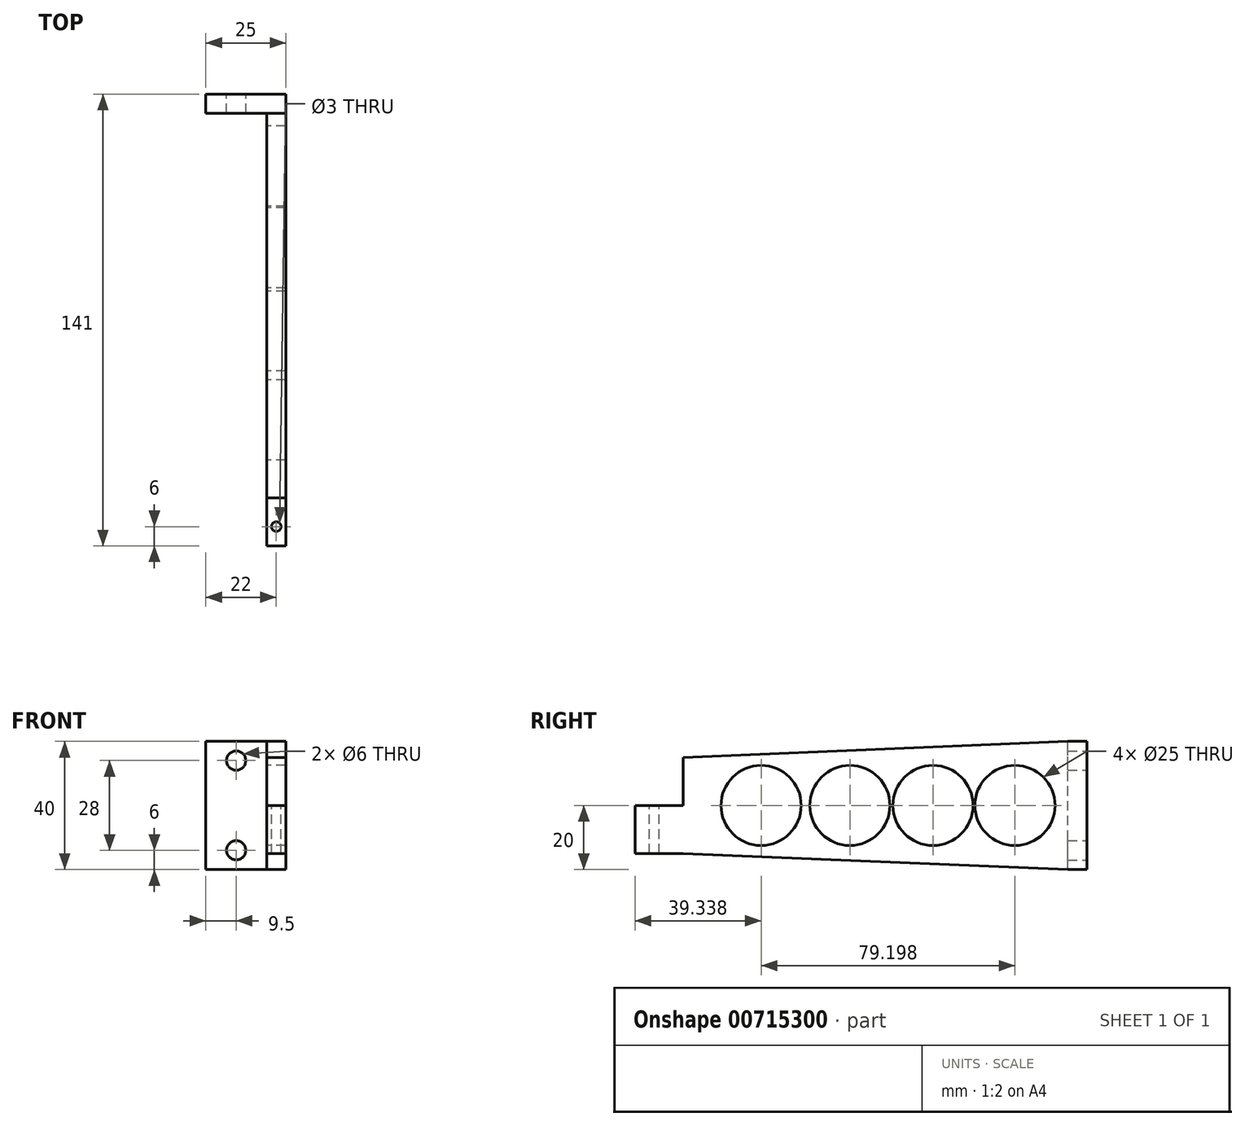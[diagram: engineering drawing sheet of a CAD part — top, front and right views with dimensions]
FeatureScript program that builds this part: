
annotation { "Feature Type Name" : "Feature", "Feature Type Description" : "" }
export const myFeature = defineFeature(function(context is Context, id is Id, definition is map)
    precondition{}
    {
        {
            var Q0;
            Q0=qCreatedBy(makeId("Front.planeOp"),FACE);
            var sketch = newSketch(context, id + "F0", { "sketchPlane" : qUnion([Q0])});
            skLineSegment(sketch, "E0.bottom", {"start": v(12.5, 20) * mm, "end": v(-12.5, 20) * mm});
            skLineSegment(sketch, "E0.top", {"start": v(12.5, -20) * mm, "end": v(-12.5, -20) * mm});
            skLineSegment(sketch, "E0.left", {"start": v(12.5, 20) * mm, "end": v(12.5, -20) * mm});
            skLineSegment(sketch, "E0.right", {"start": v(-12.5, 20) * mm, "end": v(-12.5, -20) * mm});
            skPoint(sketch, "E0.middle", {"position": v(0, 0) * mm});
            skLineSegment(sketch, "E1", {"start": v(6.5, 20) * mm, "end": v(6.5, -20) * mm, "construction": true});
            skLineSegment(sketch, "E2", {"start": v(6.5, 20) * mm, "end": v(-12.5, 20) * mm, "construction": true});
            skLineSegment(sketch, "E3", {"start": v(-3, -20) * mm, "end": v(-3, 20) * mm, "construction": true});
            skPoint(sketch, "E3.startSnap0", {"position": v(-3, 20) * mm});
            skLineSegment(sketch, "E4", {"start": v(-12.5, 14) * mm, "end": v(6.5, 14) * mm, "construction": true});
            skLineSegment(sketch, "E5", {"start": v(-12.5, -14) * mm, "end": v(6.5, -14) * mm, "construction": true});
            skCircle(sketch, "E6", {"center": v(-3, 14) * mm, "radius": 3 * mm});
            skCircle(sketch, "E7", {"center": v(-3, -14) * mm, "radius": 3 * mm});
            skSolve(sketch);
        }
        {
            var Q0;
            Q0=makeQuery(id+"F0.imprint","IMPRINT",FACE,{"disambiguationData":[TD([[makeQuery(id+"F0.imprint","IMPRINT",EDGE,{"derivedFrom":sQuery(id+"F0.wireOp",EDGE,"E0.bottom")}),1.0]])]});
            extrude(context, id + "F1", {"entities" : qUnion([Q0]), "depth" : 6 * mm, "offsetDistance" : 25.4 * mm});
        }
        {
            var Q0;
            Q0=makeQuery(id+"F1.opExtrude","CAP_FACE",FACE,{"disambiguationData":[OSD([sQuery(id+"F0.wireOp",EDGE,"E0.bottom"),sQuery(id+"F0.wireOp",EDGE,"E0.top"),sQuery(id+"F0.wireOp",EDGE,"E0.left"),sQuery(id+"F0.wireOp",EDGE,"E0.right")])],"isStart":false});
            var sketch = newSketch(context, id + "F2", { "sketchPlane" : qUnion([Q0])});
            skLineSegment(sketch, "E8", {"start": v(12.5, 20) * mm, "end": v(12.5, -20) * mm});
            skLineSegment(sketch, "E9", {"start": v(12.5, -20) * mm, "end": v(6.5, -20) * mm});
            skLineSegment(sketch, "E10", {"start": v(6.5, -20) * mm, "end": v(6.5, 20) * mm});
            skLineSegment(sketch, "E11", {"start": v(6.5, 20) * mm, "end": v(12.5, 20) * mm});
            skSolve(sketch);
        }
        {
            var Q0;
            Q0=makeQuery(id+"F2.imprint","IMPRINT",FACE,{"disambiguationData":[TD([[makeQuery(id+"F2.imprint","IMPRINT",EDGE,{"derivedFrom":sQuery(id+"F2.wireOp",EDGE,"E8")}),-1.0]])]});
            extrude(context, id + "F3", {"entities" : qUnion([Q0]), "operationType" : NewBodyOperationType.ADD, "depth" : 120 * mm, "offsetDistance" : 25.4 * mm});
        }
        {
            var Q0;
            Q0=makeQuery(id+"F3.opExtrude","SWEPT_FACE",FACE,{"disambiguationData":[OSD([sQuery(id+"F2.wireOp",EDGE,"E10")])]});
            var sketch = newSketch(context, id + "F4", { "sketchPlane" : qUnion([Q0])});
            skLineSegment(sketch, "E12", {"start": v(6, -20) * mm, "end": v(126, -15) * mm});
            skLineSegment(sketch, "E13", {"start": v(6, 20) * mm, "end": v(126, 15) * mm});
            skCircle(sketch, "E14", {"center": v(22.46, 0) * mm, "radius": 12.5 * mm});
            skCircle(sketch, "E15", {"center": v(48.04, 0) * mm, "radius": 12.5 * mm});
            skCircle(sketch, "E16", {"center": v(73.97, 0) * mm, "radius": 12.5 * mm});
            skCircle(sketch, "E17", {"center": v(101.66, 0) * mm, "radius": 12.5 * mm});
            skSolve(sketch);
        }
        {
            var Q0;
            {var subQ0=sQuery(id+"F4.wireOp",EDGE,"E13");Q0=makeQuery(id+"F4.imprint","IMPRINT",FACE,{"disambiguationData":[TD([[makeQuery(id+"F4.imprint","IMPRINT",EDGE,{"derivedFrom":subQ0}),1.0]])]});}
            var Q1;
            {var subQ0=sQuery(id+"F4.wireOp",EDGE,"E12");Q1=makeQuery(id+"F4.imprint","IMPRINT",FACE,{"disambiguationData":[TD([[makeQuery(id+"F4.imprint","IMPRINT",EDGE,{"derivedFrom":subQ0}),-1.0]])]});}
            var Q2;
            Q2=makeQuery(id+"F4.imprint","IMPRINT",FACE,{"disambiguationData":[TD([[makeQuery(id+"F4.imprint","IMPRINT",EDGE,{"derivedFrom":sQuery(id+"F4.wireOp",EDGE,"E17")}),1.0]])]});
            var Q3;
            Q3=makeQuery(id+"F4.imprint","IMPRINT",FACE,{"disambiguationData":[TD([[makeQuery(id+"F4.imprint","IMPRINT",EDGE,{"derivedFrom":sQuery(id+"F4.wireOp",EDGE,"E16")}),1.0]])]});
            var Q4;
            Q4=makeQuery(id+"F4.imprint","IMPRINT",FACE,{"disambiguationData":[TD([[makeQuery(id+"F4.imprint","IMPRINT",EDGE,{"derivedFrom":sQuery(id+"F4.wireOp",EDGE,"E15")}),1.0]])]});
            var Q5;
            Q5=makeQuery(id+"F4.imprint","IMPRINT",FACE,{"disambiguationData":[TD([[makeQuery(id+"F4.imprint","IMPRINT",EDGE,{"derivedFrom":sQuery(id+"F4.wireOp",EDGE,"E14")}),1.0]])]});
            extrude(context, id + "F5", {"entities" : qUnion([Q0, Q1, Q2, Q3, Q4, Q5]), "operationType" : NewBodyOperationType.REMOVE, "oppositeDirection" : true, "depth" : 25.4 * mm, "offsetDistance" : 25.4 * mm});
        }
        {
            var Q0;
            Q0=makeQuery(id+"F3.opExtrude","CAP_FACE",FACE,{"disambiguationData":[OSD([sQuery(id+"F2.wireOp",EDGE,"E8"),sQuery(id+"F2.wireOp",EDGE,"E9"),sQuery(id+"F2.wireOp",EDGE,"E10"),sQuery(id+"F2.wireOp",EDGE,"E11")])],"isStart":false});
            var sketch = newSketch(context, id + "F6", { "sketchPlane" : qUnion([Q0])});
            skLineSegment(sketch, "E18.bottom", {"start": v(12.5, 15) * mm, "end": v(6.5, 15) * mm});
            skLineSegment(sketch, "E18.top", {"start": v(12.5, 0) * mm, "end": v(6.5, 0) * mm});
            skLineSegment(sketch, "E18.left", {"start": v(12.5, 15) * mm, "end": v(12.5, 0) * mm});
            skLineSegment(sketch, "E18.right", {"start": v(6.5, 15) * mm, "end": v(6.5, 0) * mm});
            skSolve(sketch);
        }
        {
            var Q0;
            {var subQ0=sQuery(id+"F6.wireOp",EDGE,"E18.top");Q0=makeQuery(id+"F6.imprint","IMPRINT",FACE,{"disambiguationData":[TD([[makeQuery(id+"F6.imprint","IMPRINT",EDGE,{"derivedFrom":subQ0}),1.0]])]});}
            extrude(context, id + "F7", {"entities" : qUnion([Q0]), "operationType" : NewBodyOperationType.ADD, "depth" : 15 * mm, "offsetDistance" : 25.4 * mm});
        }
        {
            var Q0;
            Q0=makeQuery(id+"F7.opExtrude","SWEPT_FACE",FACE,{"disambiguationData":[OSD([sQuery(id+"F6.wireOp",EDGE,"E18.top")])]});
            var sketch = newSketch(context, id + "F8", { "sketchPlane" : qUnion([Q0])});
            skCircle(sketch, "E19", {"center": v(9.5, -135) * mm, "radius": 1.5 * mm});
            skPoint(sketch, "E19.centerSnap0", {"position": v(9.5, -141) * mm});
            skSolve(sketch);
        }
        {
            var Q0;
            Q0=makeQuery(id+"F8.imprint","IMPRINT",FACE,{"disambiguationData":[TD([[makeQuery(id+"F8.imprint","IMPRINT",EDGE,{"derivedFrom":sQuery(id+"F8.wireOp",EDGE,"E19")}),1.0]])]});
            extrude(context, id + "F9", {"entities" : qUnion([Q0]), "operationType" : NewBodyOperationType.REMOVE, "endBound" : BoundingType.THROUGH_ALL, "oppositeDirection" : true, "depth" : 25.4 * mm, "offsetDistance" : 25.4 * mm});
        }
    });
